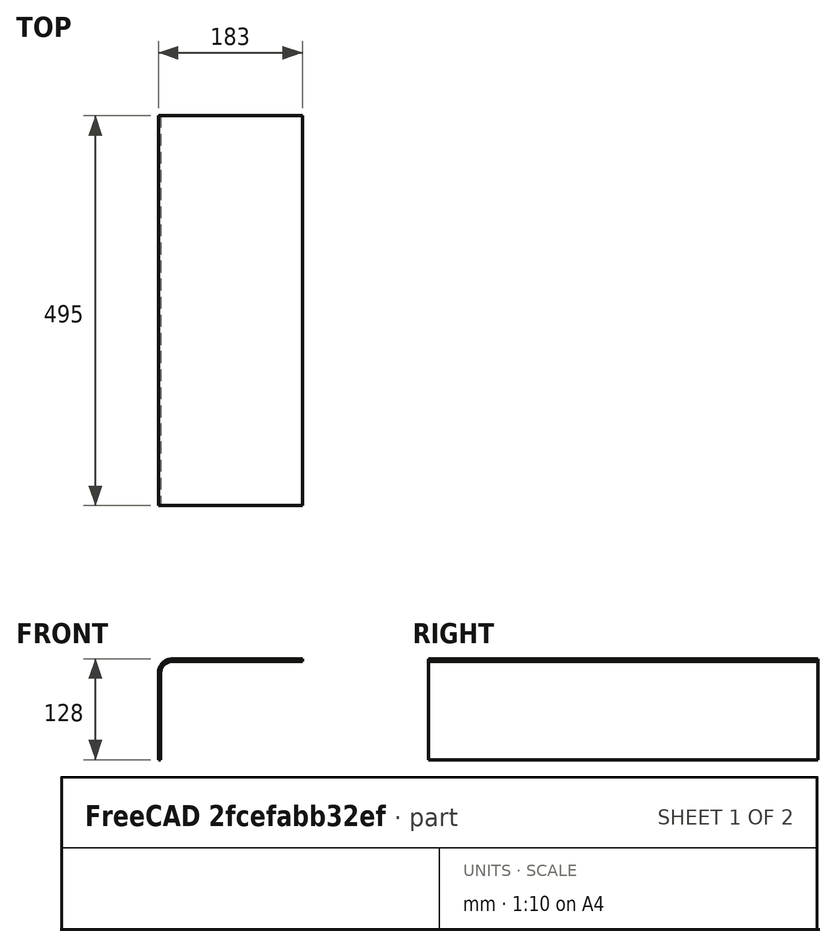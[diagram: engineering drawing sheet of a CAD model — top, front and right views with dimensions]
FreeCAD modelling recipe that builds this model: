
FCSTD DOCUMENT  (FreeCAD 0.20R29177 (Git))
Label: 1001_keyboard_Plexi_495_12
License: All rights reserved
LicenseURL: http://en.wikipedia.org/wiki/All_rights_reserved
objects: Sketcher::SketchObject×1, PartDesign::Pad×1, PartDesign::Body×1
note: 4 computed .brp shape members not serialized (recipe doc carries the construction recipe); baked Part::Feature solids carry a one-line shape summary decoded from their .brp

FEATURE [Sketcher::SketchObject] Sketch
  FullyConstrained = true
  MapMode = 5
  Placement = pos=(0,0,0) rot=(1,0,0;1.5708rad)
  Support = -> [XZ_Plane]
  sketch-geometry (8):
    g0: LineSegment StartX=7e-16 StartY=3 StartZ=0 EndX=165 EndY=3 EndZ=0
    g1: LineSegment StartX=165 StartY=3 StartZ=0 EndX=165 EndY=0 EndZ=0
    g2: LineSegment StartX=165 StartY=0 StartZ=0 EndX=0 EndY=0 EndZ=0
    g3: ArcOfCircle CenterX=0 CenterY=-15 CenterZ=0 NormalX=0 NormalY=0 NormalZ=1 AngleXU=0 Radius=15 StartAngle=1.5708 EndAngle=3.14159
    g4: ArcOfCircle CenterX=9.708e-13 CenterY=-15 CenterZ=0 NormalX=0 NormalY=0 NormalZ=1 AngleXU=0 Radius=18 StartAngle=1.5708 EndAngle=3.14159
    g5: LineSegment StartX=-15 StartY=-15 StartZ=0 EndX=-15 EndY=-125 EndZ=0
    g6: LineSegment StartX=-15 StartY=-125 StartZ=0 EndX=-18 EndY=-125 EndZ=0
    g7: LineSegment StartX=-18 StartY=-125 StartZ=0 EndX=-18 EndY=-15 EndZ=0
  constraints (23):
    c: Coincident(g0,g1)
    c: Coincident(g1,g2)
    c: Horizontal(g0)
    c: Horizontal(g2)
    c: Vertical(g1)
    c: Coincident(g2,g-1)
    c: DistanceY(g1,g1) = 3
    c: DistanceX(g0,g0) = 165
    c: Coincident(g4,g0)
    c: Coincident(g5,g6)
    c: Coincident(g6,g7)
    c: Horizontal(g6)
    c: Vertical(g5)
    c: Vertical(g7)
    c: Coincident(g7,g4)
    c: Horizontal(g4,g3)
    c: Equal(g6,g1)
    c: Radius(g3) = 15
    c: Tangent(g3,g2) = -1.5708
    c: Tangent(g5,g3) = -1.5708
    c: DistanceY(g5,g5) = 110
    c: Vertical(g2,g0)
    c: Radius(g4) = 18
FEATURE [PartDesign::Pad] Pad
  Direction = (0,-1,2e-16)
  Length = 495
  Length2 = 10
  Placement = pos=(0,0,0) rot=(1,0,0;1.5708rad)
  Profile = -> Sketch
  ReferenceAxis = -> Sketch [N_Axis]
  Type = 0
FEATURE [PartDesign::Body] Body
  Group = -> [Sketch,Pad]
  Origin = -> Origin
  Tip = -> Pad
